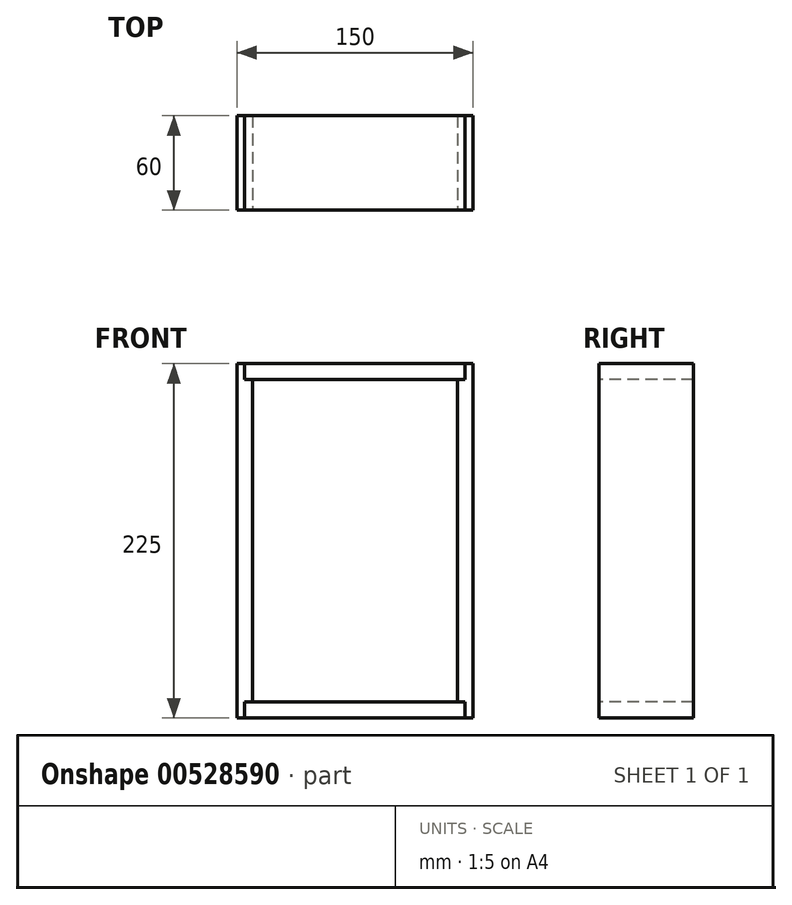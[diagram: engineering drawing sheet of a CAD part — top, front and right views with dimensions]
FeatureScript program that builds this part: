
annotation { "Feature Type Name" : "Feature", "Feature Type Description" : "" }
export const myFeature = defineFeature(function(context is Context, id is Id, definition is map)
    precondition{}
    {
        {
            var Q0;
            Q0=qCreatedBy(makeId("Front.planeOp"),FACE);
            var sketch = newSketch(context, id + "F0", { "sketchPlane" : qUnion([Q0])});
            skLineSegment(sketch, "E0", {"start": v(-75, 225) * mm, "end": v(-75, 0) * mm});
            skLineSegment(sketch, "E1", {"start": v(-75, 0) * mm, "end": v(-70, 0) * mm});
            skLineSegment(sketch, "E2", {"start": v(-70, 0) * mm, "end": v(-70, 10) * mm});
            skLineSegment(sketch, "E3", {"start": v(-70, 10) * mm, "end": v(-65, 10) * mm});
            skLineSegment(sketch, "E4", {"start": v(-65, 10) * mm, "end": v(-65, 215) * mm});
            skLineSegment(sketch, "E5", {"start": v(-65, 215) * mm, "end": v(-70, 215) * mm});
            skLineSegment(sketch, "E6", {"start": v(-70, 215) * mm, "end": v(-70, 225) * mm});
            skLineSegment(sketch, "E7", {"start": v(-70, 225) * mm, "end": v(-75, 225) * mm});
            skLineSegment(sketch, "E8", {"start": v(0, 0) * mm, "end": v(0, 138.94) * mm, "construction": true});
            skLineSegment(sketch, "E9.MirrorCS", {"start": v(75, 225) * mm, "end": v(75, 0) * mm});
            skLineSegment(sketch, "E10.MirrorCS", {"start": v(65, 10) * mm, "end": v(65, 159.04) * mm});
            skLineSegment(sketch, "E11.MirrorCS", {"start": v(70, 215) * mm, "end": v(70, 225) * mm});
            skLineSegment(sketch, "E12.MirrorCS", {"start": v(65, 215) * mm, "end": v(70, 215) * mm});
            skLineSegment(sketch, "E13.MirrorCS", {"start": v(70, 225) * mm, "end": v(75, 225) * mm});
            skLineSegment(sketch, "E14.MirrorCS", {"start": v(70, 10) * mm, "end": v(65, 10) * mm});
            skLineSegment(sketch, "E15.MirrorCS", {"start": v(70, 0) * mm, "end": v(70, 10) * mm});
            skLineSegment(sketch, "E16.MirrorCS", {"start": v(75, 0) * mm, "end": v(70, 0) * mm});
            skLineSegment(sketch, "E17", {"start": v(65, 159.04) * mm, "end": v(65, 215) * mm});
            skSolve(sketch);
        }
        {
            var Q0;
            Q0 = qSketchRegion(id + "F0", true);
            extrude(context, id + "F1", {"entities" : qUnion([Q0]), "oppositeDirection" : true, "depth" : 60 * mm, "offsetDistance" : 25 * mm});
        }
        {
            var Q0;
            Q0=qCreatedBy(makeId("Front.planeOp"),FACE);
            var sketch = newSketch(context, id + "F2", { "sketchPlane" : qUnion([Q0])});
            skLineSegment(sketch, "E18.bottom", {"start": v(-70, 0) * mm, "end": v(70, 0) * mm});
            skLineSegment(sketch, "E18.top", {"start": v(-70, 10) * mm, "end": v(70, 10) * mm});
            skLineSegment(sketch, "E18.left", {"start": v(-70, 0) * mm, "end": v(-70, 10) * mm});
            skLineSegment(sketch, "E18.right", {"start": v(70, 0) * mm, "end": v(70, 10) * mm});
            skLineSegment(sketch, "E19.bottom", {"start": v(-70, 215) * mm, "end": v(70, 215) * mm});
            skLineSegment(sketch, "E19.top", {"start": v(-70, 225) * mm, "end": v(70, 225) * mm});
            skLineSegment(sketch, "E19.left", {"start": v(-70, 215) * mm, "end": v(-70, 225) * mm});
            skLineSegment(sketch, "E19.right", {"start": v(70, 215) * mm, "end": v(70, 225) * mm});
            skSolve(sketch);
        }
        {
            var Q0;
            Q0 = qSketchRegion(id + "F2", true);
            extrude(context, id + "F3", {"entities" : qUnion([Q0]), "oppositeDirection" : true, "depth" : 60 * mm, "offsetDistance" : 25 * mm});
        }
    });
